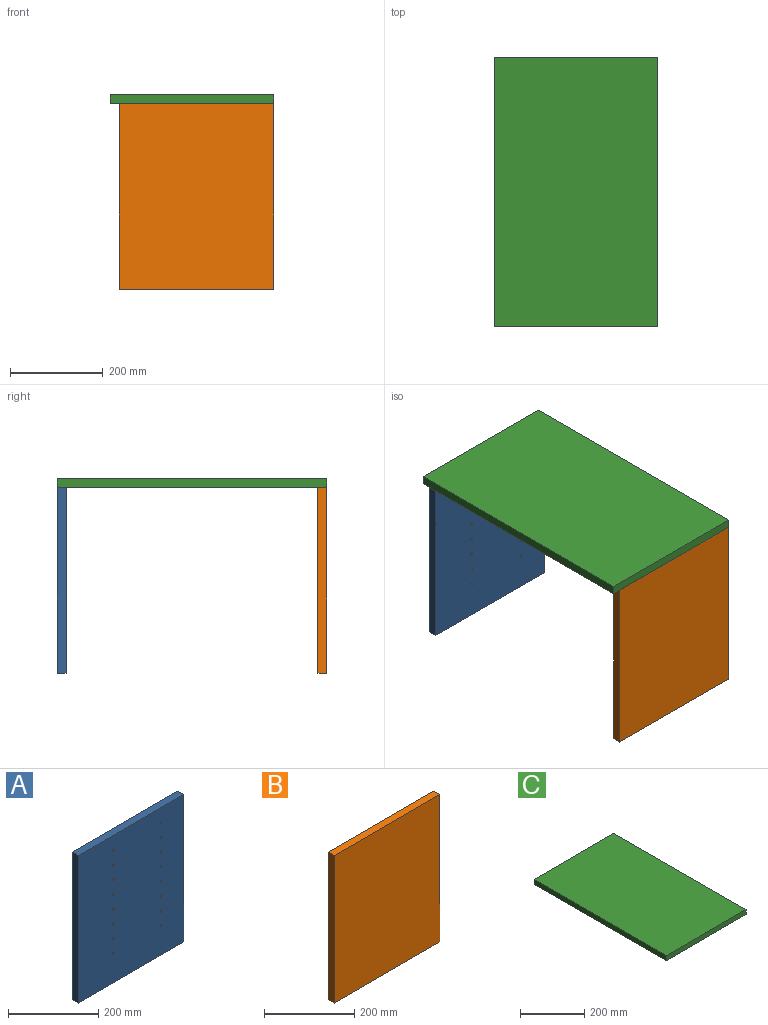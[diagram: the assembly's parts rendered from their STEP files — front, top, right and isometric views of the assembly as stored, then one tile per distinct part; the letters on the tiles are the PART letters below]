
ASSEMBLY  parts=3 mates=1
PART A: 38 faces, bbox 332x19x400 mm
  f0: plane 332x19mm, normal (0,0,1), area 6308mm2, adj f1,f3,f4,f5
  f1: plane 400x19mm, normal (-1,0,0), area 7600mm2, adj f0,f2,f4,f5
  f2: plane 332x19mm, normal (0,0,-1), area 6308mm2, adj f1,f3,f4,f5
  f3: plane 400x19mm, normal (1,0,0), area 7600mm2, adj f0,f2,f4,f5
  f4: plane 400x332mm, normal (0,-1,0), area 132347.6mm2, adj f0,f1,f2,f3,f6,f8,f10,f12
  f5: plane 400x332mm, normal (0,1,0), area 132800mm2, adj f0,f1,f2,f3
  f6: cylinder r=3mm len=15mm, axis (0,-1,0), area 282.7mm2, adj f4,f7
  f7: plane 6x6mm, normal (0,-1,0), area 28.3mm2, adj f6
  f8: cylinder r=3mm len=15mm, axis (0,-1,0), area 282.7mm2, adj f4,f9
  f9: plane 6x6mm, normal (0,-1,0), area 28.3mm2, adj f8
  f10: cylinder r=3mm len=15mm, axis (0,-1,0), area 282.7mm2, adj f4,f11
  f11: plane 6x6mm, normal (0,-1,0), area 28.3mm2, adj f10
  f12: cylinder r=3mm len=15mm, axis (0,-1,0), area 282.7mm2, adj f4,f13
  f13: plane 6x6mm, normal (0,-1,0), area 28.3mm2, adj f12
  f14: cylinder r=3mm len=15mm, axis (0,-1,0), area 282.7mm2, adj f4,f15
  f15: plane 6x6mm, normal (0,-1,0), area 28.3mm2, adj f14
  f16: cylinder r=3mm len=15mm, axis (0,-1,0), area 282.7mm2, adj f4,f17
  f17: plane 6x6mm, normal (0,-1,0), area 28.3mm2, adj f16
  f18: cylinder r=3mm len=15mm, axis (0,-1,0), area 282.7mm2, adj f4,f19
  f19: plane 6x6mm, normal (0,-1,0), area 28.3mm2, adj f18
  f20: cylinder r=3mm len=15mm, axis (0,-1,0), area 282.7mm2, adj f4,f21
  f21: plane 6x6mm, normal (0,-1,0), area 28.3mm2, adj f20
  f22: cylinder r=3mm len=15mm, axis (0,-1,0), area 282.7mm2, adj f4,f23
  f23: plane 6x6mm, normal (0,-1,0), area 28.3mm2, adj f22
  f24: cylinder r=3mm len=15mm, axis (0,-1,0), area 282.7mm2, adj f4,f25
  f25: plane 6x6mm, normal (0,-1,0), area 28.3mm2, adj f24
  f26: cylinder r=3mm len=15mm, axis (0,-1,0), area 282.7mm2, adj f4,f27
  f27: plane 6x6mm, normal (0,-1,0), area 28.3mm2, adj f26
  f28: cylinder r=3mm len=15mm, axis (0,-1,0), area 282.7mm2, adj f4,f29
  f29: plane 6x6mm, normal (0,-1,0), area 28.3mm2, adj f28
  f30: cylinder r=3mm len=15mm, axis (0,-1,0), area 282.7mm2, adj f4,f31
  f31: plane 6x6mm, normal (0,-1,0), area 28.3mm2, adj f30
  f32: cylinder r=3mm len=15mm, axis (0,-1,0), area 282.7mm2, adj f4,f33
  f33: plane 6x6mm, normal (0,-1,0), area 28.3mm2, adj f32
  f34: cylinder r=3mm len=15mm, axis (0,-1,0), area 282.7mm2, adj f4,f35
  f35: plane 6x6mm, normal (0,-1,0), area 28.3mm2, adj f34
  f36: cylinder r=3mm len=15mm, axis (0,-1,0), area 282.7mm2, adj f4,f37
  f37: plane 6x6mm, normal (0,-1,0), area 28.3mm2, adj f36
PART B: 38 faces, bbox 332x19x400 mm
  f0: plane 332x19mm, normal (0,0,1), area 6308mm2, adj f1,f3,f4,f5
  f1: plane 400x19mm, normal (-1,0,0), area 7600mm2, adj f0,f2,f4,f5
  f2: plane 332x19mm, normal (0,0,-1), area 6308mm2, adj f1,f3,f4,f5
  f3: plane 400x19mm, normal (1,0,0), area 7600mm2, adj f0,f2,f4,f5
  f4: plane 400x332mm, normal (0,1,0), area 132347.6mm2, adj f0,f1,f2,f3,f6,f8,f10,f12
  f5: plane 400x332mm, normal (0,-1,0), area 132800mm2, adj f0,f1,f2,f3
  f6: cylinder r=3mm len=15mm, axis (0,1,0), area 282.7mm2, adj f4,f7
  f7: plane 6x6mm, normal (0,1,0), area 28.3mm2, adj f6
  f8: cylinder r=3mm len=15mm, axis (0,1,0), area 282.7mm2, adj f4,f9
  f9: plane 6x6mm, normal (0,1,0), area 28.3mm2, adj f8
  f10: cylinder r=3mm len=15mm, axis (0,1,0), area 282.7mm2, adj f4,f11
  f11: plane 6x6mm, normal (0,1,0), area 28.3mm2, adj f10
  f12: cylinder r=3mm len=15mm, axis (0,1,0), area 282.7mm2, adj f4,f13
  f13: plane 6x6mm, normal (0,1,0), area 28.3mm2, adj f12
  f14: cylinder r=3mm len=15mm, axis (0,1,0), area 282.7mm2, adj f4,f15
  f15: plane 6x6mm, normal (0,1,0), area 28.3mm2, adj f14
  f16: cylinder r=3mm len=15mm, axis (0,1,0), area 282.7mm2, adj f4,f17
  f17: plane 6x6mm, normal (0,1,0), area 28.3mm2, adj f16
  f18: cylinder r=3mm len=15mm, axis (0,1,0), area 282.7mm2, adj f4,f19
  f19: plane 6x6mm, normal (0,1,0), area 28.3mm2, adj f18
  f20: cylinder r=3mm len=15mm, axis (0,1,0), area 282.7mm2, adj f4,f21
  f21: plane 6x6mm, normal (0,1,0), area 28.3mm2, adj f20
  f22: cylinder r=3mm len=15mm, axis (0,1,0), area 282.7mm2, adj f4,f23
  f23: plane 6x6mm, normal (0,1,0), area 28.3mm2, adj f22
  f24: cylinder r=3mm len=15mm, axis (0,1,0), area 282.7mm2, adj f4,f25
  f25: plane 6x6mm, normal (0,1,0), area 28.3mm2, adj f24
  f26: cylinder r=3mm len=15mm, axis (0,1,0), area 282.7mm2, adj f4,f27
  f27: plane 6x6mm, normal (0,1,0), area 28.3mm2, adj f26
  f28: cylinder r=3mm len=15mm, axis (0,1,0), area 282.7mm2, adj f4,f29
  f29: plane 6x6mm, normal (0,1,0), area 28.3mm2, adj f28
  f30: cylinder r=3mm len=15mm, axis (0,1,0), area 282.7mm2, adj f4,f31
  f31: plane 6x6mm, normal (0,1,0), area 28.3mm2, adj f30
  f32: cylinder r=3mm len=15mm, axis (0,1,0), area 282.7mm2, adj f4,f33
  f33: plane 6x6mm, normal (0,1,0), area 28.3mm2, adj f32
  f34: cylinder r=3mm len=15mm, axis (0,1,0), area 282.7mm2, adj f4,f35
  f35: plane 6x6mm, normal (0,1,0), area 28.3mm2, adj f34
  f36: cylinder r=3mm len=15mm, axis (0,1,0), area 282.7mm2, adj f4,f37
  f37: plane 6x6mm, normal (0,1,0), area 28.3mm2, adj f36
PART C: 6 faces, bbox 351x580x19 mm
  f0: plane 580x19mm, normal (1,0,0), area 11020mm2, adj f1,f3,f4,f5
  f1: plane 351x19mm, normal (0,1,0), area 6669mm2, adj f0,f2,f4,f5
  f2: plane 580x19mm, normal (-1,0,0), area 11020mm2, adj f1,f3,f4,f5
  f3: plane 351x19mm, normal (0,-1,0), area 6669mm2, adj f0,f2,f4,f5
  f4: plane 580x351mm, normal (0,0,1), area 203580mm2, adj f0,f1,f2,f3
  f5: plane 580x351mm, normal (0,0,-1), area 203580mm2, adj f0,f1,f2,f3
PLACE A t=(0,-3,0)mm
PLACE B at identity
PLACE C t=(75,-564,569)mm
MATE fastened C.f5 <-> B.f0  axis (0,0,1) through (407,-583,569)mm
